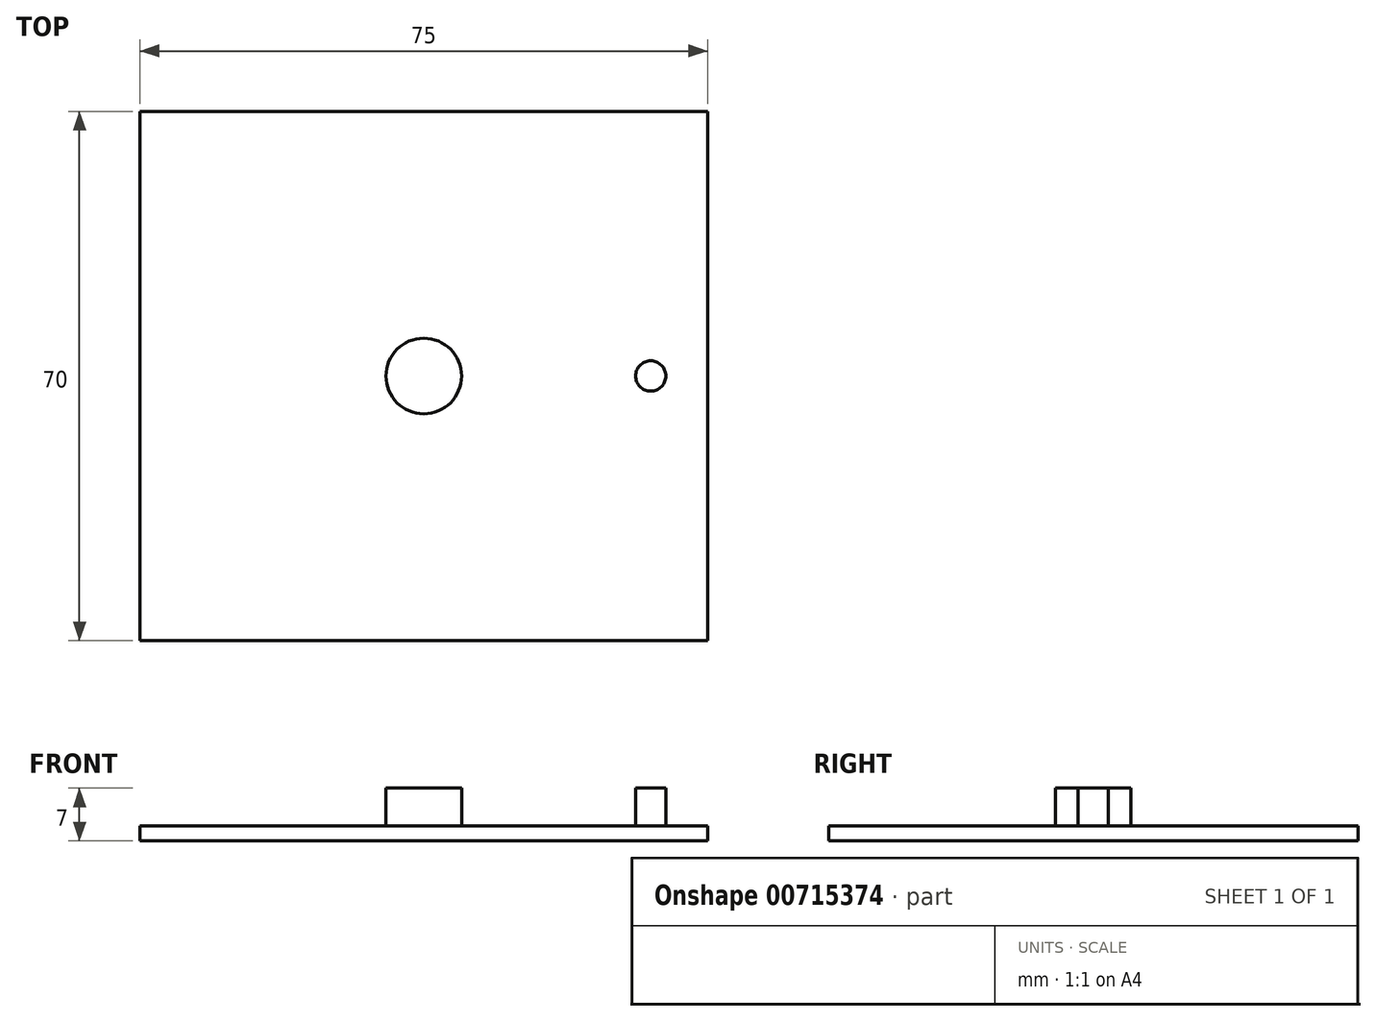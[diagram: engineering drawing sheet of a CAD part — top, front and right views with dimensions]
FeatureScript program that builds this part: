
annotation { "Feature Type Name" : "Feature", "Feature Type Description" : "" }
export const myFeature = defineFeature(function(context is Context, id is Id, definition is map)
    precondition{}
    {
        {
            var Q0;
            Q0=qCreatedBy(makeId("Top.planeOp"),FACE);
            var sketch = newSketch(context, id + "F0", { "sketchPlane" : qUnion([Q0])});
            skLineSegment(sketch, "E0.bottom", {"start": v(-32.78, 35) * mm, "end": v(42.22, 35) * mm});
            skLineSegment(sketch, "E0.top", {"start": v(-32.78, -35) * mm, "end": v(42.22, -35) * mm});
            skLineSegment(sketch, "E0.left", {"start": v(-32.78, 35) * mm, "end": v(-32.78, -35) * mm});
            skLineSegment(sketch, "E0.right", {"start": v(42.22, 35) * mm, "end": v(42.22, -35) * mm});
            skLineSegment(sketch, "E1", {"start": v(-32.78, 0) * mm, "end": v(42.22, 0) * mm, "construction": true});
            skPoint(sketch, "E1.endSnap0", {"position": v(42.22, 0) * mm});
            skCircle(sketch, "E2", {"center": v(4.72, 0) * mm, "radius": 5 * mm});
            skCircle(sketch, "E3", {"center": v(34.72, 0) * mm, "radius": 2 * mm});
            skSolve(sketch);
        }
        {
            var Q0;
            Q0=makeQuery(id+"F0.imprint","IMPRINT",FACE,{"disambiguationData":[TD([[makeQuery(id+"F0.imprint","IMPRINT",EDGE,{"derivedFrom":sQuery(id+"F0.wireOp",EDGE,"E0.bottom")}),-1.0]])]});
            extrude(context, id + "F1", {"entities" : qUnion([Q0]), "depth" : 2 * mm, "offsetDistance" : 25.4 * mm});
        }
        {
            var Q0;
            Q0=makeQuery(id+"F0.imprint","IMPRINT",FACE,{"disambiguationData":[TD([[makeQuery(id+"F0.imprint","IMPRINT",EDGE,{"derivedFrom":sQuery(id+"F0.wireOp",EDGE,"E2")}),1.0]])]});
            var Q1;
            Q1=makeQuery(id+"F0.imprint","IMPRINT",FACE,{"disambiguationData":[TD([[makeQuery(id+"F0.imprint","IMPRINT",EDGE,{"derivedFrom":sQuery(id+"F0.wireOp",EDGE,"E3")}),1.0]])]});
            extrude(context, id + "F2", {"entities" : qUnion([Q0, Q1]), "operationType" : NewBodyOperationType.ADD, "depth" : 7 * mm, "offsetDistance" : 25.4 * mm});
        }
    });
